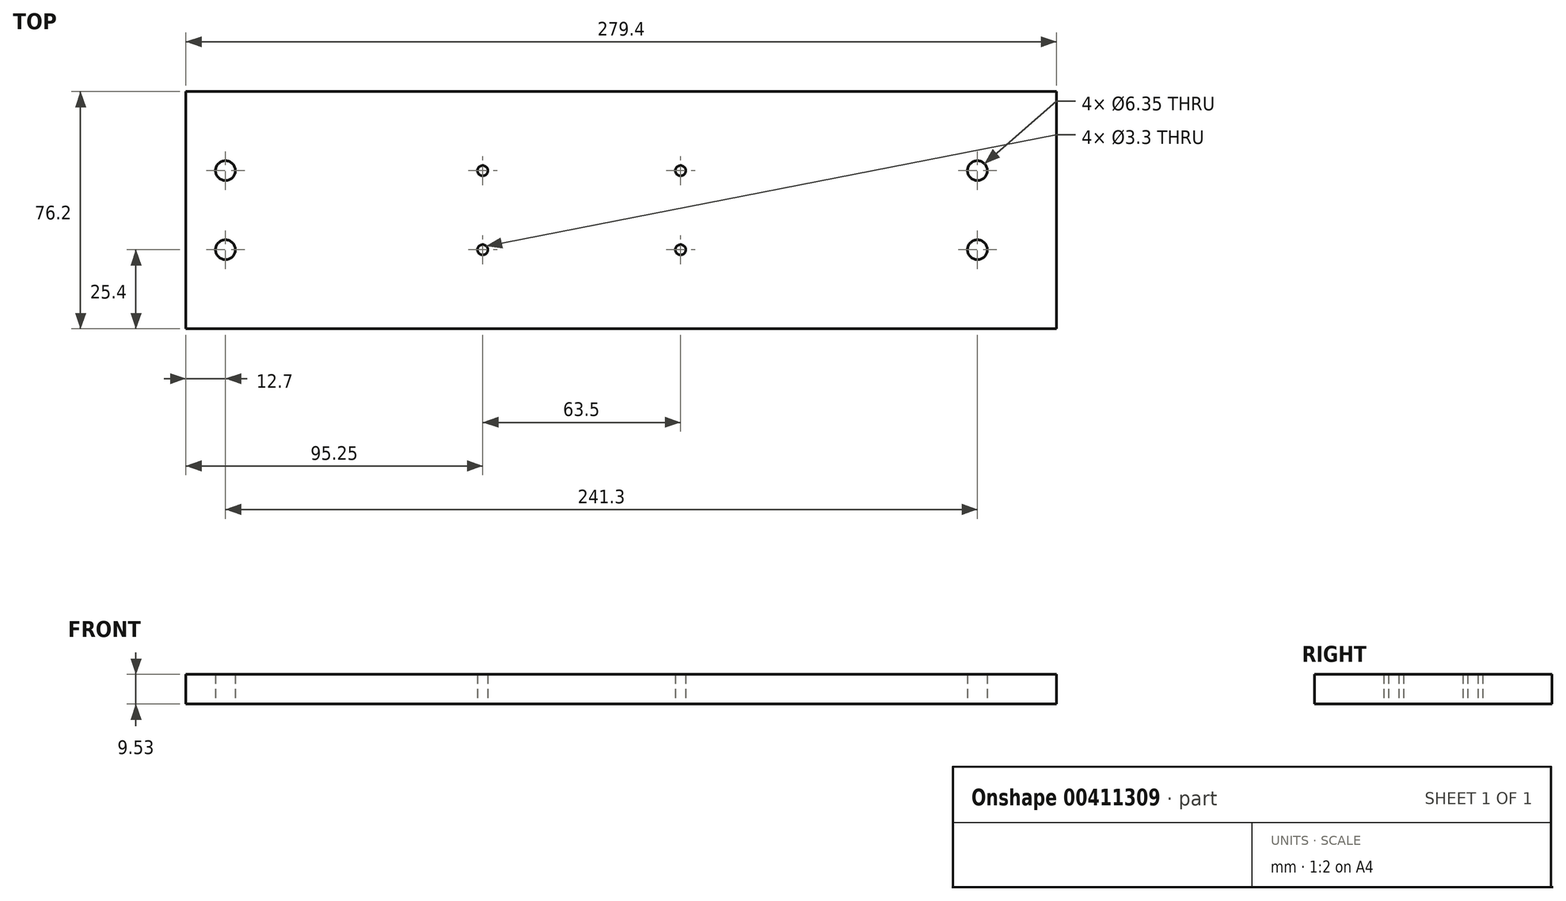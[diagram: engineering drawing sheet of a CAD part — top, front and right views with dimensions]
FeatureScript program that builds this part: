
annotation { "Feature Type Name" : "Feature", "Feature Type Description" : "" }
export const myFeature = defineFeature(function(context is Context, id is Id, definition is map)
    precondition{}
    {
        {
            var Q0;
            Q0=qCreatedBy(makeId("Top.planeOp"),FACE);
            var sketch = newSketch(context, id + "F0", { "sketchPlane" : qUnion([Q0])});
            skLineSegment(sketch, "E0.bottom", {"start": v(-139.7, 38.1) * mm, "end": v(139.7, 38.1) * mm});
            skLineSegment(sketch, "E0.top", {"start": v(-139.7, -38.1) * mm, "end": v(139.7, -38.1) * mm});
            skLineSegment(sketch, "E0.left", {"start": v(-139.7, 38.1) * mm, "end": v(-139.7, -38.1) * mm});
            skLineSegment(sketch, "E0.right", {"start": v(139.7, 38.1) * mm, "end": v(139.7, -38.1) * mm});
            skCircle(sketch, "E1", {"center": v(-127, 12.7) * mm, "radius": 3.18 * mm});
            skCircle(sketch, "E2", {"center": v(-127, -12.7) * mm, "radius": 3.18 * mm});
            skCircle(sketch, "E3", {"center": v(-44.45, 12.7) * mm, "radius": 1.65 * mm});
            skCircle(sketch, "E4", {"center": v(19.05, 12.7) * mm, "radius": 1.65 * mm});
            skCircle(sketch, "E5", {"center": v(114.3, 12.7) * mm, "radius": 3.18 * mm});
            skCircle(sketch, "E6.MirrorC", {"center": v(-44.45, -12.7) * mm, "radius": 1.65 * mm});
            skCircle(sketch, "E7.MirrorC", {"center": v(19.05, -12.7) * mm, "radius": 1.65 * mm});
            skCircle(sketch, "E8.MirrorC", {"center": v(114.3, -12.7) * mm, "radius": 3.18 * mm});
            skSolve(sketch);
        }
        {
            var Q0;
            Q0 = qSketchRegion(id + "F0", true);
            extrude(context, id + "F1", {"entities" : qUnion([Q0]), "depth" : 9.52 * mm});
        }
    });
